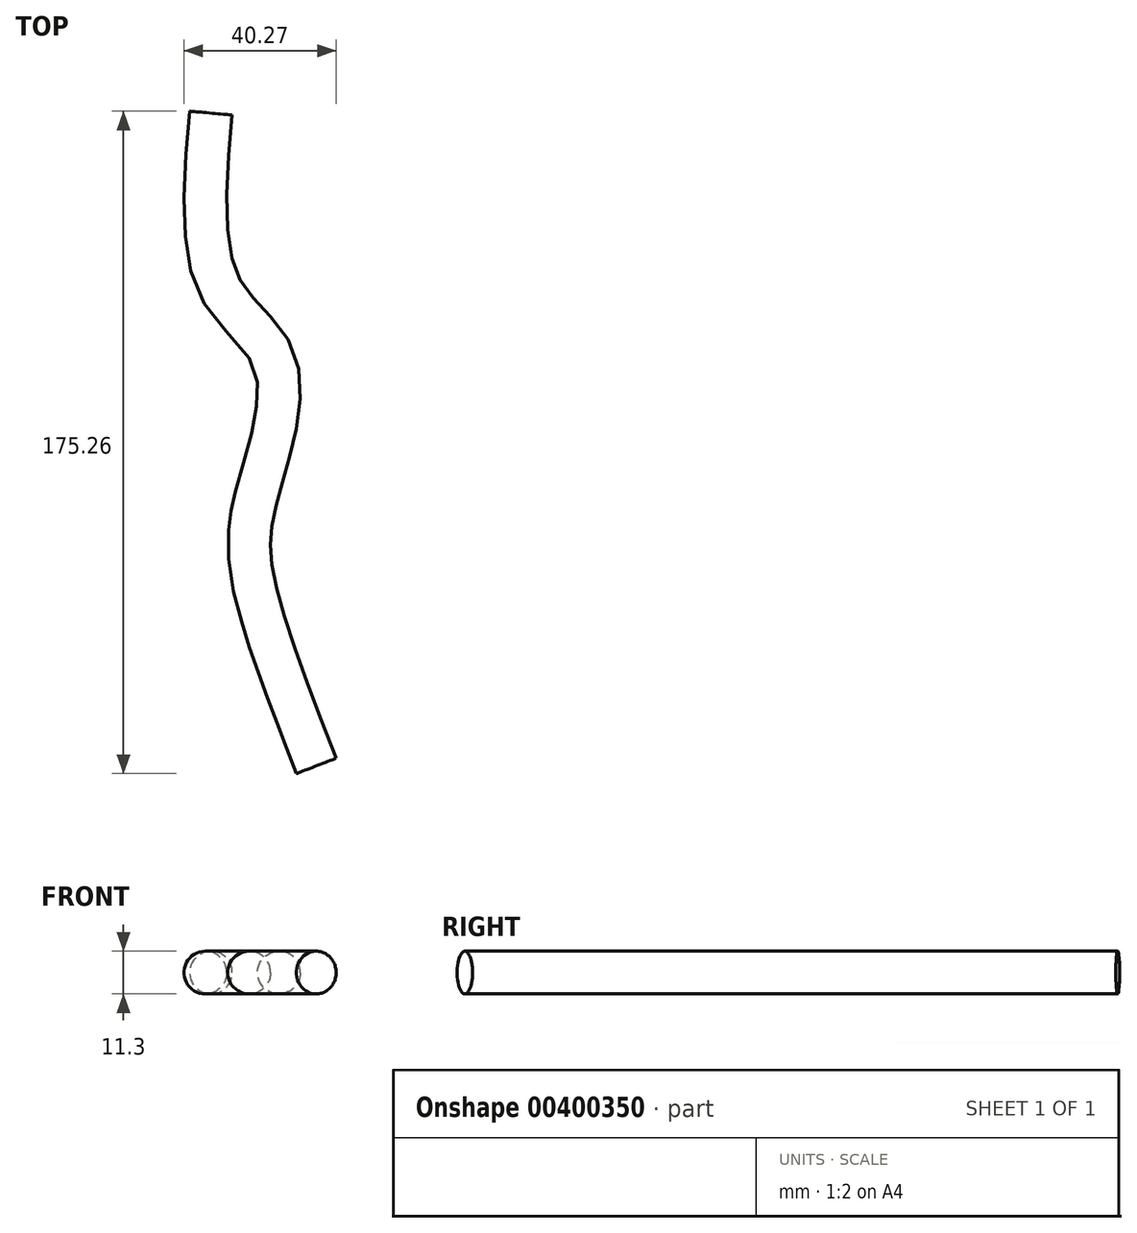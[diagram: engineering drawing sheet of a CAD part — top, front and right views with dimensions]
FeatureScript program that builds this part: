
annotation { "Feature Type Name" : "Feature", "Feature Type Description" : "" }
export const myFeature = defineFeature(function(context is Context, id is Id, definition is map)
    precondition{}
    {
        {
            var Q0;
            Q0=qCreatedBy(makeId("Top.planeOp"),FACE);
            var sketch = newSketch(context, id + "F0", { "sketchPlane" : qUnion([Q0])});
            skFitSpline(sketch, "E0", {"points": [v(-16.14, 86.56) * mm, v(-13.93, 40.6) * mm, v(0, 22.57) * mm, v(0, 0) * mm, v(-5.55, -21.53) * mm, v(-4.1, -41.14) * mm, v(11.74, -86.28) * mm], "startDerivative": vector(-22.32, -252.13) * mm, "endDerivative": vector(90.27, -233.1) * mm});
            skSolve(sketch);
        }
        {
            var Q0;
            Q0=sQuery(id+"F0.wireOp",EDGE,"E0");
            var Q1;
            Q1=sQuery(id+"F0.wireOp",VERTEX,"E0.6.internal");
            cPlane(context, id + "F1", {"entities" : qUnion([Q0, Q1]), "cplaneType" : CPlaneType.CURVE_POINT, "offset" : 25.4 * mm, "width" : 152.4 * mm, "height" : 152.4 * mm});
        }
        {
            var Q0;
            Q0=qCreatedBy(id+"F1.planeOp",FACE);
            var sketch = newSketch(context, id + "F2", { "sketchPlane" : qUnion([Q0])});
            skCircle(sketch, "E1", {"center": v(-19.93, 0) * mm, "radius": 5.65 * mm});
            skSolve(sketch);
        }
        {
            var Q0;
            Q0=makeQuery(id+"F2.imprint","IMPRINT",FACE,{"disambiguationData":[TD([[makeQuery(id+"F2.imprint","IMPRINT",EDGE,{"derivedFrom":sQuery(id+"F2.wireOp",EDGE,"E1")}),1.0]])]});
            var Q1;
            Q1=sQuery(id+"F0.wireOp",EDGE,"E0");
            sweep(context, id + "F3", {"profiles" : qUnion([Q0]), "path" : qUnion([Q1])});
        }
    });
